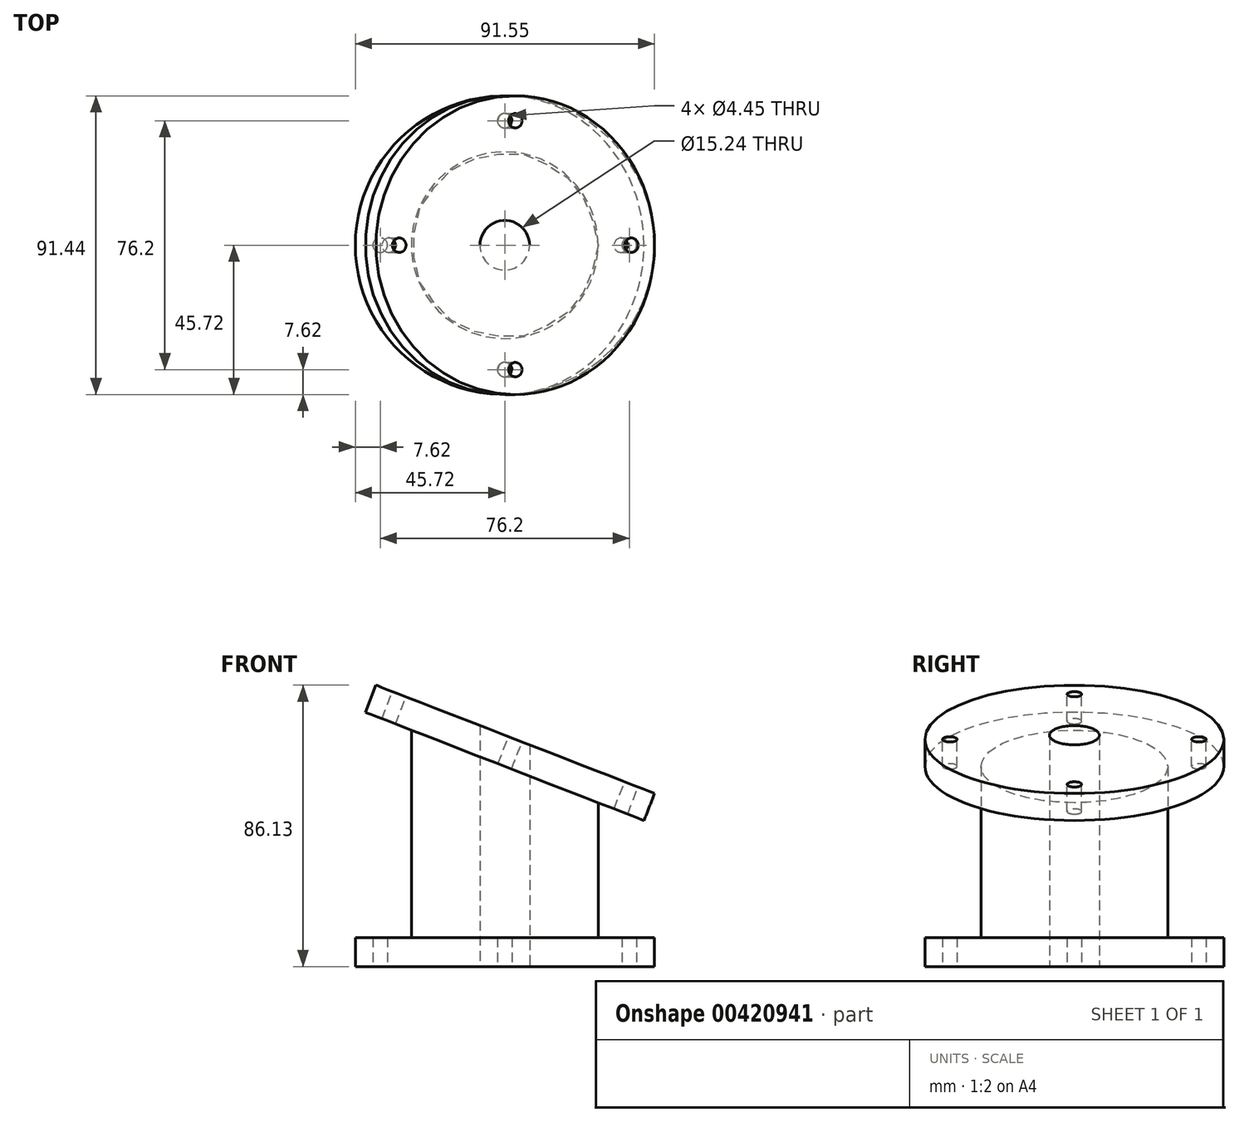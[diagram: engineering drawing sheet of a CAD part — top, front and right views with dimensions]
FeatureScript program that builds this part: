
annotation { "Feature Type Name" : "Feature", "Feature Type Description" : "" }
export const myFeature = defineFeature(function(context is Context, id is Id, definition is map)
    precondition{}
    {
        {
            var Q0;
            Q0=qCreatedBy(makeId("Top.planeOp"),FACE);
            var sketch = newSketch(context, id + "F0", { "sketchPlane" : qUnion([Q0])});
            skCircle(sketch, "E0", {"center": v(0, 0) * mm, "radius": 45.72 * mm});
            skSolve(sketch);
        }
        {
            var Q0;
            Q0 = qSketchRegion(id + "F0", true);
            extrude(context, id + "F1", {"entities" : qUnion([Q0]), "depth" : 8.9 * mm});
        }
        {
            var Q0;
            Q0=makeQuery(id+"F1.opExtrude","CAP_FACE",FACE,{"disambiguationData":[OSD([sQuery(id+"F0.wireOp",EDGE,"E0")])],"isStart":false});
            var sketch = newSketch(context, id + "F2", { "sketchPlane" : qUnion([Q0])});
            skCircle(sketch, "E1", {"center": v(0, 0) * mm, "radius": 28.57 * mm});
            skSolve(sketch);
        }
        {
            var Q0;
            Q0 = qSketchRegion(id + "F2", true);
            extrude(context, id + "F3", {"entities" : qUnion([Q0]), "operationType" : NewBodyOperationType.ADD, "depth" : 63.5 * mm});
        }
        {
            var Q0;
            Q0=qCreatedBy(makeId("Front.planeOp"),FACE);
            var sketch = newSketch(context, id + "F4", { "sketchPlane" : qUnion([Q0])});
            skLineSegment(sketch, "E2.0", {"start": v(-28.57, 72.39) * mm, "end": v(28.57, 72.39) * mm});
            skLineSegment(sketch, "E3", {"start": v(-28.58, 72.4) * mm, "end": v(28.58, 50.16) * mm});
            skLineSegment(sketch, "E4", {"start": v(28.57, 72.39) * mm, "end": v(28.58, 50.16) * mm});
            skSolve(sketch);
        }
        {
            var Q0;
            Q0 = qSketchRegion(id + "F4", true);
            extrude(context, id + "F5", {"entities" : qUnion([Q0]), "operationType" : NewBodyOperationType.REMOVE, "endBound" : BoundingType.THROUGH_ALL, "oppositeDirection" : true, "depth" : 25.4 * mm, "hasSecondDirection" : true, "secondDirectionBound" : SecondDirectionBoundingType.THROUGH_ALL, "secondDirectionOppositeDirection" : false, "secondDirectionDepth" : 25.4 * mm});
        }
        {
            var Q0;
            Q0=makeQuery(id+"F5.boolean.opBoolean","COPY",FACE,{"derivedFrom":makeQuery(id+"F5.opExtrude","SWEPT_FACE",FACE,{"disambiguationData":[OSD([sQuery(id+"F4.wireOp",EDGE,"E3")])]})});
            var sketch = newSketch(context, id + "F6", { "sketchPlane" : qUnion([Q0])});
            skCircle(sketch, "E5", {"center": v(-22.2, 0) * mm, "radius": 45.72 * mm});
            skSolve(sketch);
        }
        {
            var Q0;
            Q0 = qSketchRegion(id + "F6", true);
            extrude(context, id + "F7", {"entities" : qUnion([Q0]), "operationType" : NewBodyOperationType.ADD, "depth" : 8.9 * mm});
        }
        {
            var Q0;
            Q0=makeQuery(id+"F1.opExtrude","CAP_FACE",FACE,{"disambiguationData":[OSD([sQuery(id+"F0.wireOp",EDGE,"E0")])],"isStart":true});
            var sketch = newSketch(context, id + "F8", { "sketchPlane" : qUnion([Q0])});
            skCircle(sketch, "E6", {"center": v(0, 0) * mm, "radius": 7.62 * mm});
            skSolve(sketch);
        }
        {
            var Q0;
            Q0 = qSketchRegion(id + "F8", true);
            extrude(context, id + "F9", {"entities" : qUnion([Q0]), "operationType" : NewBodyOperationType.REMOVE, "endBound" : BoundingType.THROUGH_ALL, "oppositeDirection" : true, "depth" : 25.4 * mm});
        }
        {
            var Q0;
            Q0=makeQuery(id+"F1.opExtrude","CAP_FACE",FACE,{"disambiguationData":[OSD([sQuery(id+"F0.wireOp",EDGE,"E0")])],"isStart":true});
            var sketch = newSketch(context, id + "F10", { "sketchPlane" : qUnion([Q0])});
            skCircle(sketch, "E7", {"center": v(0, 0) * mm, "radius": 38.1 * mm, "construction": true});
            skCircle(sketch, "E8", {"center": v(0, -38.1) * mm, "radius": 2.22 * mm});
            skCircle(sketch, "E9", {"center": v(38.1, 0) * mm, "radius": 2.22 * mm});
            skCircle(sketch, "E10", {"center": v(0, 38.1) * mm, "radius": 2.22 * mm});
            skCircle(sketch, "E11", {"center": v(-38.1, 0) * mm, "radius": 2.22 * mm});
            skSolve(sketch);
        }
        {
            var Q0;
            Q0 = qSketchRegion(id + "F10", true);
            extrude(context, id + "F11", {"entities" : qUnion([Q0]), "operationType" : NewBodyOperationType.REMOVE, "endBound" : BoundingType.UP_TO_NEXT, "oppositeDirection" : true, "depth" : 25.4 * mm});
        }
        {
            var Q0;
            Q0=makeQuery(id+"F7.opExtrude","CAP_FACE",FACE,{"disambiguationData":[OSD([sQuery(id+"F6.wireOp",EDGE,"E5")])],"isStart":false});
            var sketch = newSketch(context, id + "F12", { "sketchPlane" : qUnion([Q0])});
            skLineSegment(sketch, "E12", {"start": v(23.51, 0) * mm, "end": v(-67.93, 0) * mm, "construction": true});
            skLineSegment(sketch, "E13", {"start": v(-22.2, 0) * mm, "end": v(-22.2, -45.72) * mm, "construction": true});
            skCircle(sketch, "E14", {"center": v(-22.2, 0) * mm, "radius": 38.1 * mm, "construction": true});
            skCircle(sketch, "E15", {"center": v(-22.2, -38.1) * mm, "radius": 2.22 * mm});
            skCircle(sketch, "E16", {"center": v(15.9, 0) * mm, "radius": 2.22 * mm});
            skCircle(sketch, "E17", {"center": v(-60.3, 0) * mm, "radius": 2.22 * mm});
            skLineSegment(sketch, "E18", {"start": v(-22.2, 0) * mm, "end": v(-22.2, 38.1) * mm, "construction": true});
            skCircle(sketch, "E19", {"center": v(-22.2, 38.1) * mm, "radius": 2.22 * mm});
            skSolve(sketch);
        }
        {
            var Q0;
            Q0 = qSketchRegion(id + "F12", true);
            extrude(context, id + "F13", {"entities" : qUnion([Q0]), "operationType" : NewBodyOperationType.REMOVE, "endBound" : BoundingType.UP_TO_NEXT, "oppositeDirection" : true, "depth" : 25.4 * mm});
        }
    });
